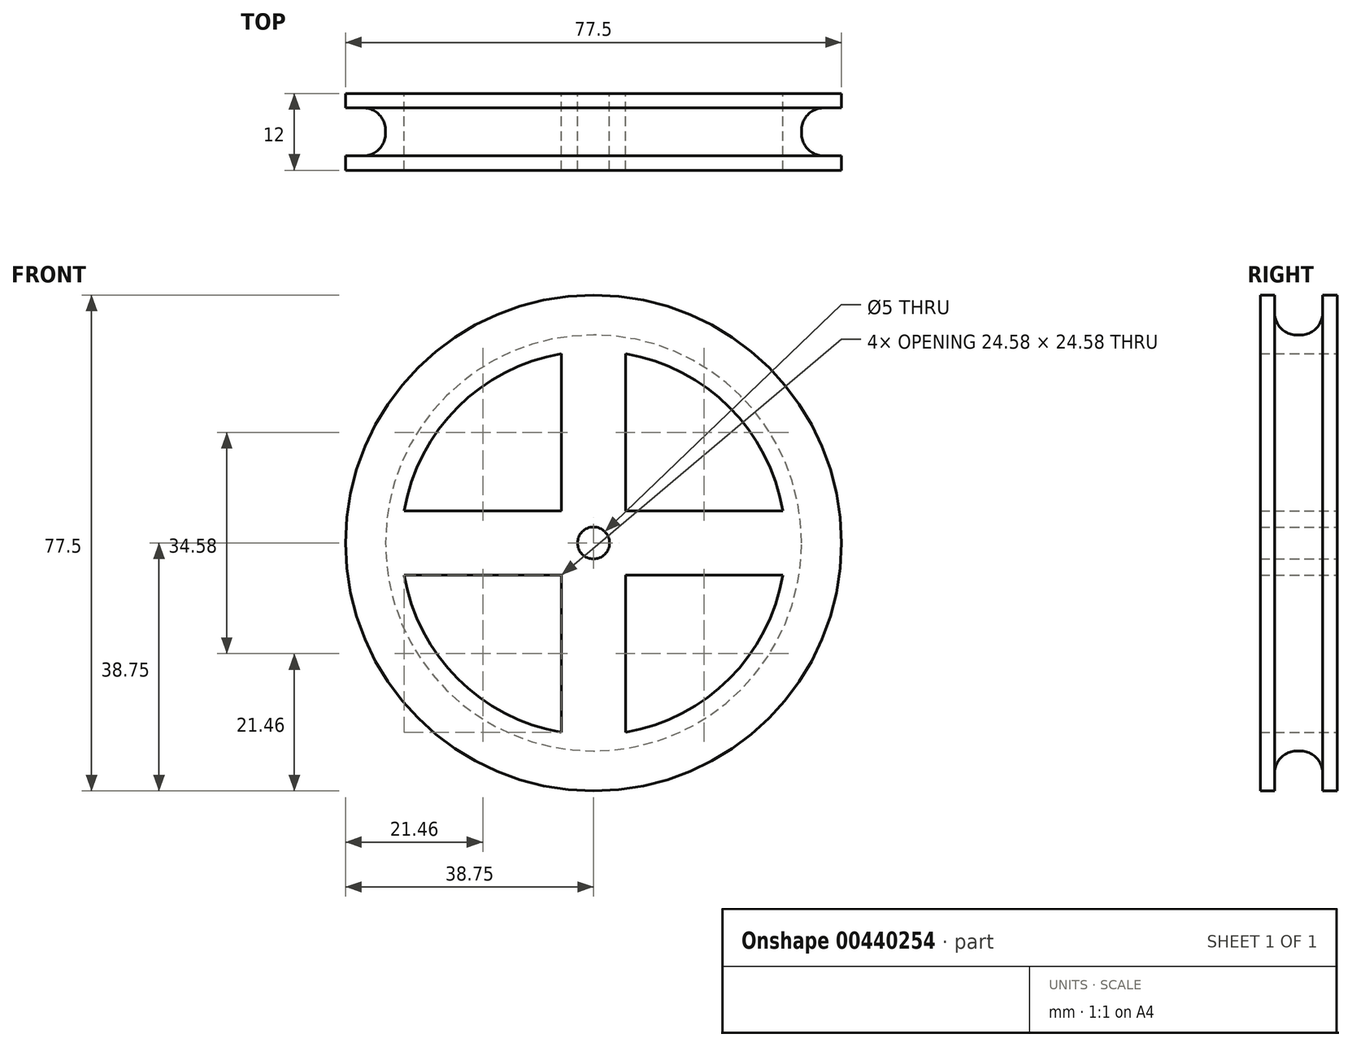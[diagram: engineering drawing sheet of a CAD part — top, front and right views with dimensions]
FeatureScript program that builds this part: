
annotation { "Feature Type Name" : "Feature", "Feature Type Description" : "" }
export const myFeature = defineFeature(function(context is Context, id is Id, definition is map)
    precondition{}
    {
        {
            var Q0;
            Q0=qCreatedBy(makeId("Front.planeOp"),FACE);
            var sketch = newSketch(context, id + "F0", { "sketchPlane" : qUnion([Q0])});
            skCircle(sketch, "E0", {"center": v(0, 0) * mm, "radius": 38.75 * mm});
            skCircle(sketch, "E1", {"center": v(0, 0) * mm, "radius": 30 * mm});
            skLineSegment(sketch, "E2", {"start": v(5, 29.58) * mm, "end": v(5, -29.58) * mm});
            skLineSegment(sketch, "E3", {"start": v(-5, 29.58) * mm, "end": v(-5, -29.58) * mm});
            skLineSegment(sketch, "E4", {"start": v(29.58, 5) * mm, "end": v(-29.58, 5) * mm});
            skLineSegment(sketch, "E5", {"start": v(29.58, -5) * mm, "end": v(-29.58, -5) * mm});
            skSolve(sketch);
        }
        {
            var Q0;
            Q0=qCreatedBy(makeId("Right.planeOp"),FACE);
            var sketch = newSketch(context, id + "F1", { "sketchPlane" : qUnion([Q0])});
            skLineSegment(sketch, "E6.bottom", {"start": v(3.75, 40) * mm, "end": v(-3.75, 40) * mm});
            skLineSegment(sketch, "E6.top", {"start": v(0.25, 32.5) * mm, "end": v(-0.25, 32.5) * mm});
            skLineSegment(sketch, "E6.left", {"start": v(3.75, 40) * mm, "end": v(3.75, 36) * mm});
            skLineSegment(sketch, "E6.right", {"start": v(-3.75, 40) * mm, "end": v(-3.75, 36) * mm});
            skPoint(sketch, "E7.visualSharp", {"position": v(-3.75, 32.5) * mm});
            skArc(sketch, "E7.filletArc", {"start": v(-3.75, 36) * mm, "mid": v(-2.72, 33.53) * mm, "end": v(-0.25, 32.5) * mm});
            skPoint(sketch, "E8.visualSharp", {"position": v(3.75, 32.5) * mm});
            skArc(sketch, "E8.filletArc", {"start": v(0.25, 32.5) * mm, "mid": v(2.72, 33.53) * mm, "end": v(3.75, 36) * mm});
            skSolve(sketch);
        }
        {
            var Q0;
            Q0=qCreatedBy(makeId("Top.planeOp"),FACE);
            var sketch = newSketch(context, id + "F2", { "sketchPlane" : qUnion([Q0])});
            skLineSegment(sketch, "E9", {"start": v(0, 51.52) * mm, "end": v(0, -55.54) * mm});
            skSolve(sketch);
        }
        {
            var Q0;
            Q0=makeQuery(id+"F0.imprint","IMPRINT",FACE,{"disambiguationData":[TD([[makeQuery(id+"F0.imprint","IMPRINT",EDGE,{"derivedFrom":sQuery(id+"F0.wireOp",EDGE,"E0")}),1.0]])]});
            var Q1;
            {var subQ0=sQuery(id+"F0.wireOp",EDGE,"E2");var subQ1=sQuery(id+"F0.wireOp",EDGE,"E1");var subQ2=makeQuery(id+"F0.imprint","INTERSECT",VERTEX,{"disambiguationData":[OD(0.0)],"derivedFrom":[subQ1,subQ0]});Q1=makeQuery(id+"F0.imprint","IMPRINT",FACE,{"disambiguationData":[TD([[makeQuery(id+"F0.imprint","IMPRINT",EDGE,{"disambiguationData":[TD([[subQ2,-1.0]])],"derivedFrom":subQ1}),1.0]])]});}
            var Q2;
            {var subQ0=sQuery(id+"F0.wireOp",EDGE,"E4");var subQ1=sQuery(id+"F0.wireOp",EDGE,"E1");var subQ2=makeQuery(id+"F0.imprint","INTERSECT",VERTEX,{"disambiguationData":[OD(0.0)],"derivedFrom":[subQ1,subQ0]});Q2=makeQuery(id+"F0.imprint","IMPRINT",FACE,{"disambiguationData":[TD([[makeQuery(id+"F0.imprint","IMPRINT",EDGE,{"disambiguationData":[TD([[subQ2,1.0]])],"derivedFrom":subQ1}),1.0]])]});}
            var Q3;
            {var subQ0=sQuery(id+"F0.wireOp",EDGE,"E4");var subQ1=sQuery(id+"F0.wireOp",EDGE,"E2");var subQ2=makeQuery(id+"F0.imprint","INTERSECT",VERTEX,{"derivedFrom":[subQ1,subQ0]});Q3=makeQuery(id+"F0.imprint","IMPRINT",FACE,{"disambiguationData":[TD([[makeQuery(id+"F0.imprint","IMPRINT",EDGE,{"disambiguationData":[TD([[subQ2,-1.0]])],"derivedFrom":subQ1}),-1.0]])]});}
            var Q4;
            {var subQ0=sQuery(id+"F0.wireOp",EDGE,"E4");var subQ1=sQuery(id+"F0.wireOp",EDGE,"E1");var subQ2=makeQuery(id+"F0.imprint","INTERSECT",VERTEX,{"disambiguationData":[OD(1.0)],"derivedFrom":[subQ1,subQ0]});Q4=makeQuery(id+"F0.imprint","IMPRINT",FACE,{"disambiguationData":[TD([[makeQuery(id+"F0.imprint","IMPRINT",EDGE,{"disambiguationData":[TD([[subQ2,-1.0]])],"derivedFrom":subQ1}),1.0]])]});}
            var Q5;
            {var subQ0=sQuery(id+"F0.wireOp",EDGE,"E2");var subQ1=sQuery(id+"F0.wireOp",EDGE,"E1");var subQ2=makeQuery(id+"F0.imprint","INTERSECT",VERTEX,{"disambiguationData":[OD(1.0)],"derivedFrom":[subQ1,subQ0]});Q5=makeQuery(id+"F0.imprint","IMPRINT",FACE,{"disambiguationData":[TD([[makeQuery(id+"F0.imprint","IMPRINT",EDGE,{"disambiguationData":[TD([[subQ2,1.0]])],"derivedFrom":subQ1}),1.0]])]});}
            extrude(context, id + "F3", {"entities" : qUnion([Q0, Q1, Q2, Q3, Q4, Q5]), "endBound" : BoundingType.SYMMETRIC, "depth" : 12 * mm});
        }
        {
            var Q0;
            Q0 = qSketchRegion(id + "F1", true);
            var Q1;
            Q1=sQuery(id+"F2.wireOp",EDGE,"E9");
            revolve(context, id + "F4", {"operationType" : NewBodyOperationType.REMOVE, "entities" : qUnion([Q0]), "axis" : qUnion([Q1]), "revolveType" : RevolveType.FULL});
        }
        {
            var Q0;
            Q0=qCreatedBy(makeId("Front.planeOp"),FACE);
            var sketch = newSketch(context, id + "F5", { "sketchPlane" : qUnion([Q0])});
            skCircle(sketch, "E10", {"center": v(0, 0) * mm, "radius": 2.5 * mm});
            skSolve(sketch);
        }
        {
            var Q0;
            Q0 = qSketchRegion(id + "F5", true);
            extrude(context, id + "F6", {"entities" : qUnion([Q0]), "operationType" : NewBodyOperationType.REMOVE, "endBound" : BoundingType.SYMMETRIC, "depth" : 25 * mm});
        }
    });
